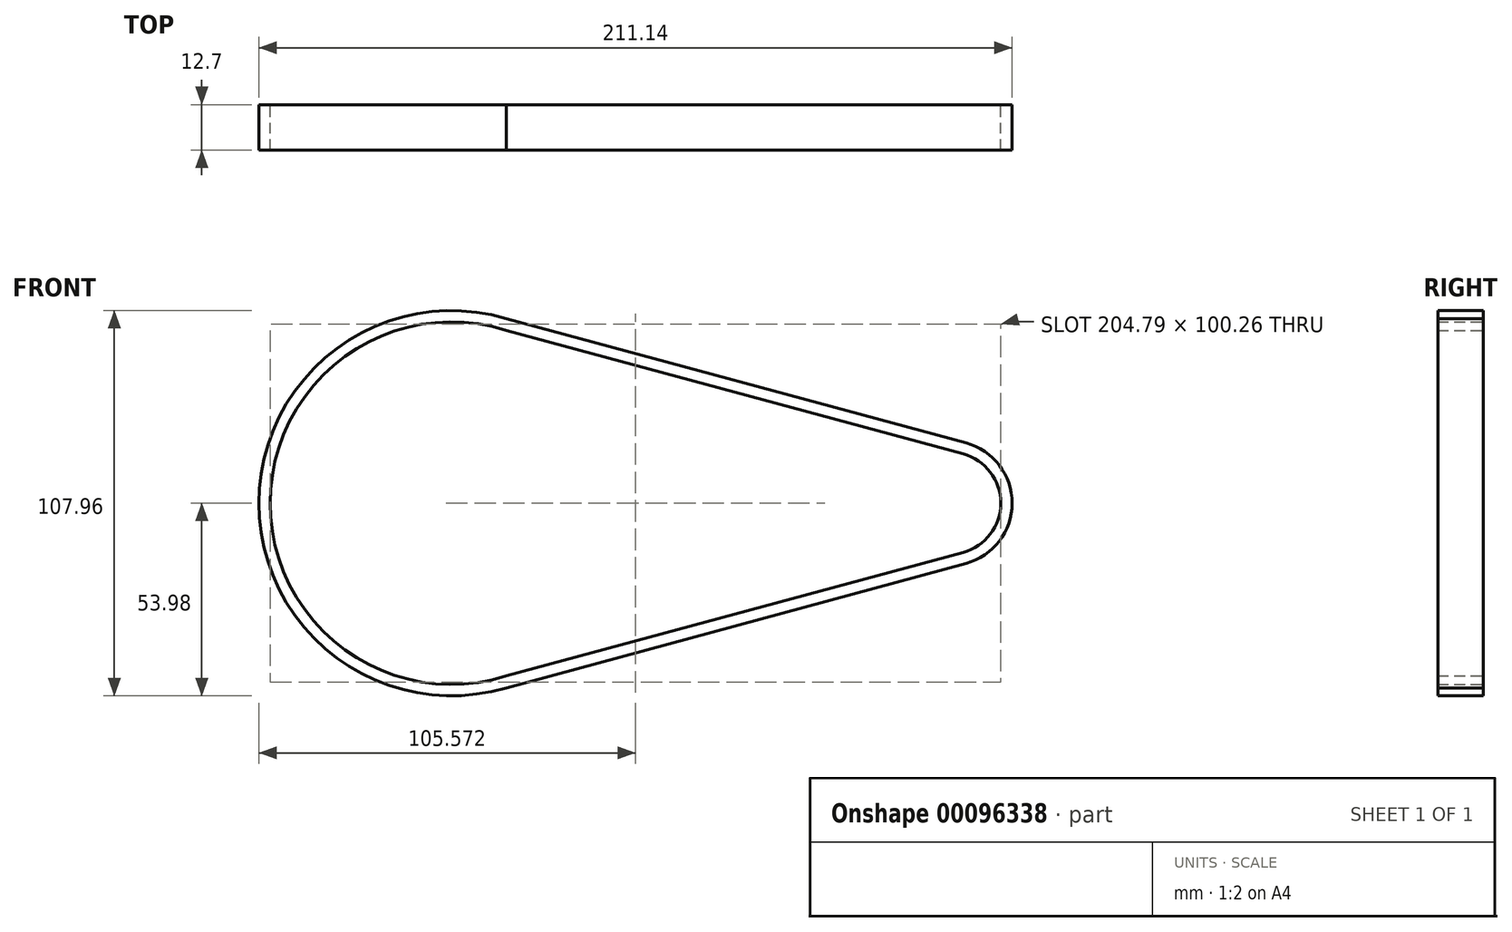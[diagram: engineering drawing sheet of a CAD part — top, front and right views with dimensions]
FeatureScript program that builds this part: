
annotation { "Feature Type Name" : "Feature", "Feature Type Description" : "" }
export const myFeature = defineFeature(function(context is Context, id is Id, definition is map)
    precondition{}
    {
        {
            var Q0;
            Q0=qCreatedBy(makeId("Front.planeOp"),FACE);
            var sketch = newSketch(context, id + "F0", { "sketchPlane" : qUnion([Q0])});
            skArc(sketch, "E0", {"start": v(-75.82, 48.42) * mm, "mid": v(-141.97, 0) * mm, "end": v(-75.82, -48.42) * mm});
            skArc(sketch, "E1", {"start": v(52.26, -13.8) * mm, "mid": v(62.82, 0) * mm, "end": v(52.26, 13.8) * mm});
            skLineSegment(sketch, "E2", {"start": v(-80.03, 49.56) * mm, "end": v(52.26, 13.8) * mm});
            skLineSegment(sketch, "E3", {"start": v(-80.03, -49.56) * mm, "end": v(52.26, -13.8) * mm});
            skArc(sketch, "E4", {"start": v(-75.82, 51.74) * mm, "mid": v(-145.15, 0) * mm, "end": v(-75.82, -51.74) * mm});
            skArc(sketch, "E5", {"start": v(53.1, -16.86) * mm, "mid": v(66, 0) * mm, "end": v(53.1, 16.86) * mm});
            skLineSegment(sketch, "E6", {"start": v(-75.82, 51.74) * mm, "end": v(53.1, 16.86) * mm});
            skLineSegment(sketch, "E7", {"start": v(-75.82, -51.74) * mm, "end": v(53.1, -16.86) * mm});
            skSolve(sketch);
        }
        {
            var Q0;
            Q0 = qSketchRegion(id + "F0", true);
            extrude(context, id + "F1", {"entities" : qUnion([Q0]), "depth" : 12.7 * mm});
        }
    });
